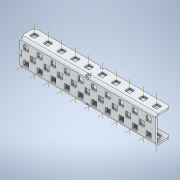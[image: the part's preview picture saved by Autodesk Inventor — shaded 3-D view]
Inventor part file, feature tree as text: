
AUTODESK INVENTOR PART (.ipt)
format: ipt  version: 2020 (Build 240168000, 168)  size: 1,213,440 bytes
history: native  units: in
note: dims shown in document units (in); Inventor stores cm internally (conversion verified against a paired STEP export)
features: other x53, plane x8, pattern_linear x4, split x2, sheet_metal_op x1
ambient origin geometry x8: Origin, YZ Plane, XZ Plane, XY Plane, X Axis, Y Axis, Z Axis, Center Point
bodies: Solid1 (feature_tree)
feature tree (68):
  other  "Work Axis1"
  pattern_linear  "Rectangular Pattern1"  Count1=10 Spacing1=0.5in
  other  "Work Axis72"
  pattern_linear  "Rectangular Pattern2"  Count1=10 Spacing1=0.5in
  pattern_linear  "Rectangular Pattern3"  Count1=10 Spacing1=0.5in
  other  "Work Axis141"
  pattern_linear  "Rectangular Pattern4"  Count1=9 Spacing1=0.5in
  plane  "Work Plane7"
  split  "Split1"
  plane  "Work Plane8"
  split  "Split2"
  plane  "Work Plane1"
  plane  "Work Plane2"
  other  "Work Point1"
  other  "Work Axis2"
  other  "Work Axis3"
  other  "Work Axis4"
  other  "Work Axis5"
  other  "Work Axis6"
  other  "Work Axis7"
  other  "Work Axis8"
  other  "Work Axis9"
  other  "Work Axis10"
  other  "Work Axis36"
  other  "Work Axis37"
  other  "Work Axis38"
  other  "Work Axis39"
  other  "Work Axis40"
  other  "Work Axis41"
  other  "Work Axis42"
  other  "Work Axis43"
  other  "Work Axis44"
  other  "Work Axis45"
  plane  "Work Plane3"
  plane  "Work Plane4"
  other  "Work Point2"
  other  "Work Axis71"
  other  "Work Point3"
  other  "Work Axis73"
  other  "Work Axis74"
  other  "Work Axis75"
  other  "Work Axis76"
  other  "Work Axis77"
  other  "Work Axis78"
  other  "Work Axis79"
  other  "Work Axis80"
  other  "Work Axis81"
  other  "Work Axis107"
  other  "Work Axis108"
  other  "Work Axis109"
  other  "Work Axis110"
  plane  "Work Plane5"
  plane  "Work Plane6"
  other  "Work Point4"
  other  "Work Axis142"
  other  "Work Axis143"
  other  "Work Axis144"
  other  "Work Axis145"
  other  "Work Axis146"
  other  "Work Axis147"
  other  "Work Axis148"
  other  "Work Axis149"
  other  "Work Axis175"
  other  "Work Axis176"
  other  "Work Axis177"
  other  "Work Axis178"
  other  "Work Axis179"
  sheet_metal_op  "Fold1"
